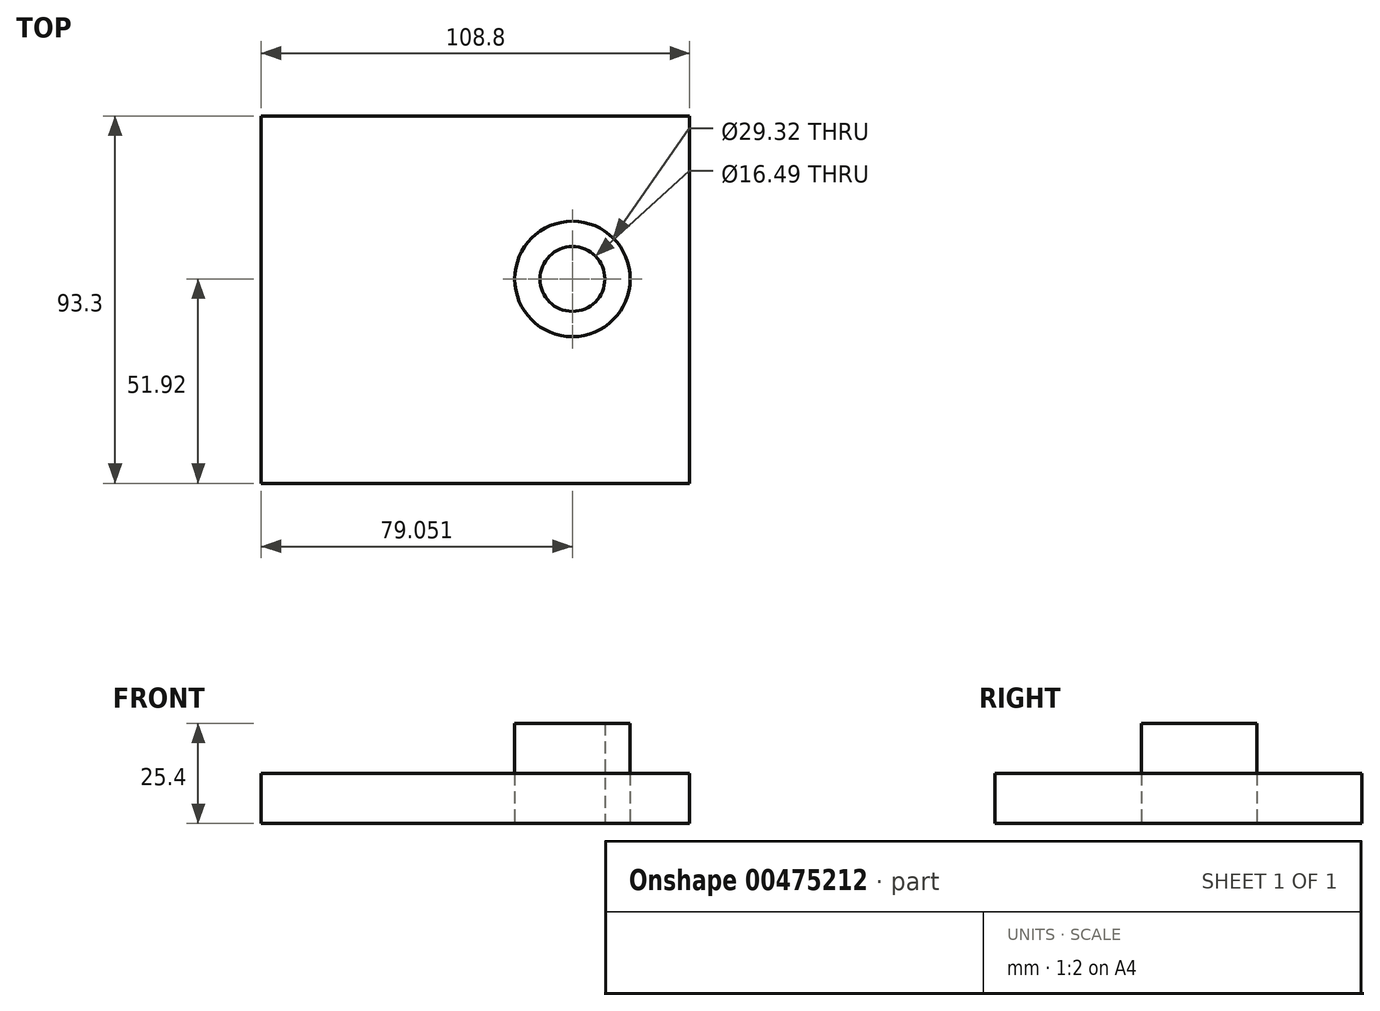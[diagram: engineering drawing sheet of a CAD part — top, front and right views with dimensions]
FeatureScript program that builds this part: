
annotation { "Feature Type Name" : "Feature", "Feature Type Description" : "" }
export const myFeature = defineFeature(function(context is Context, id is Id, definition is map)
    precondition{}
    {
        {
            var Q0;
            Q0=qCreatedBy(makeId("Top.planeOp"),FACE);
            var sketch = newSketch(context, id + "F0", { "sketchPlane" : qUnion([Q0])});
            skLineSegment(sketch, "E0.bottom", {"start": v(-121.61, 41.38) * mm, "end": v(-12.81, 41.38) * mm});
            skLineSegment(sketch, "E0.top", {"start": v(-121.61, -51.92) * mm, "end": v(-12.81, -51.92) * mm});
            skLineSegment(sketch, "E0.left", {"start": v(-121.61, 41.38) * mm, "end": v(-121.61, -51.92) * mm});
            skLineSegment(sketch, "E0.right", {"start": v(-12.81, 41.38) * mm, "end": v(-12.81, -51.92) * mm});
            skCircle(sketch, "E1", {"center": v(-42.56, 0) * mm, "radius": 14.66 * mm});
            skCircle(sketch, "E2", {"center": v(-42.56, 0) * mm, "radius": 8.25 * mm});
            skSolve(sketch);
        }
        {
            var Q0;
            Q0=makeQuery(id+"F0.imprint","IMPRINT",FACE,{"disambiguationData":[TD([[makeQuery(id+"F0.imprint","IMPRINT",EDGE,{"derivedFrom":sQuery(id+"F0.wireOp",EDGE,"E1")}),1.0]])]});
            extrude(context, id + "F1", {"entities" : qUnion([Q0]), "depth" : 25.4 * mm});
        }
        {
            var Q0;
            Q0=makeQuery(id+"F0.imprint","IMPRINT",FACE,{"disambiguationData":[TD([[makeQuery(id+"F0.imprint","IMPRINT",EDGE,{"derivedFrom":sQuery(id+"F0.wireOp",EDGE,"E0.bottom")}),-1.0]])]});
            extrude(context, id + "F2", {"entities" : qUnion([Q0]), "depth" : 12.7 * mm});
        }
    });
